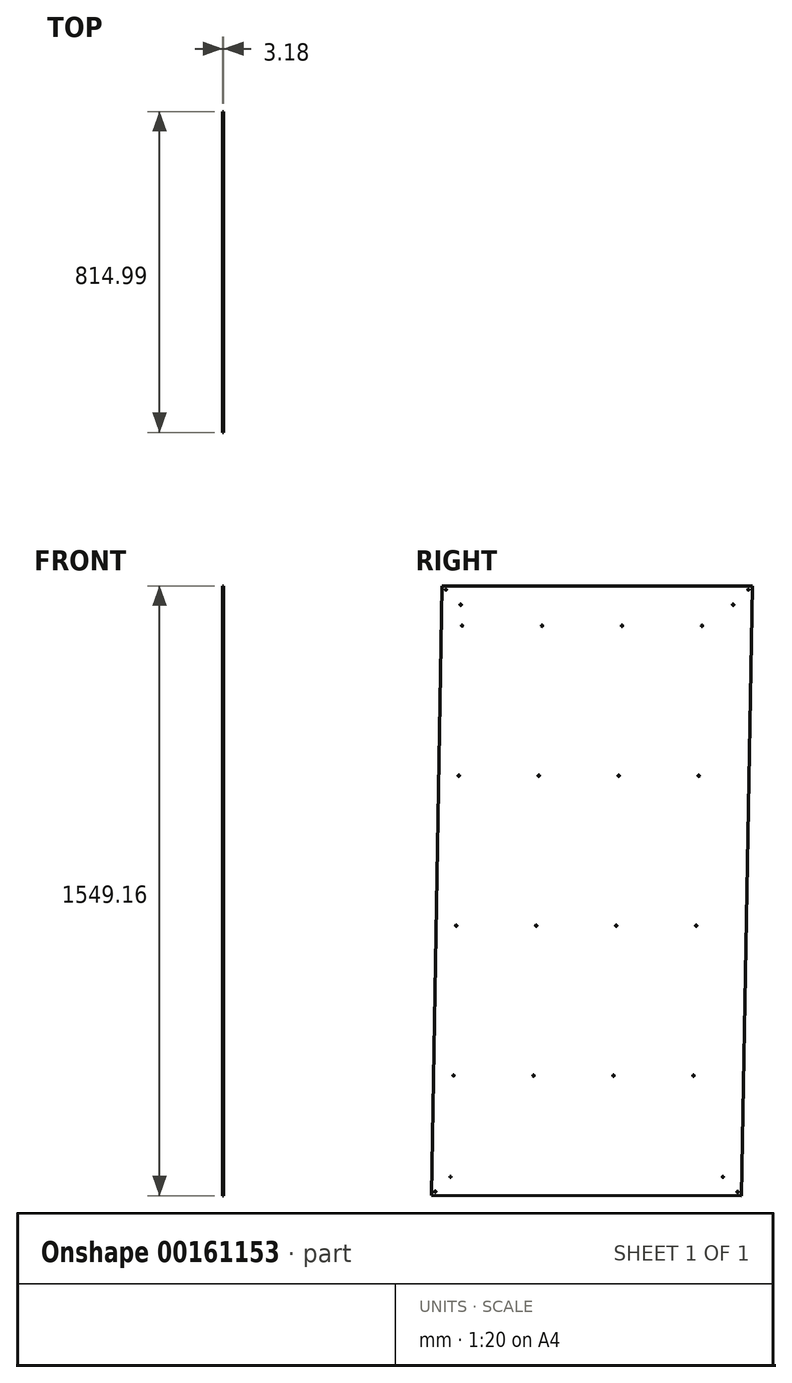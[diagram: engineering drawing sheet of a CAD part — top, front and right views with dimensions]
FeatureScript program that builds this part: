
annotation { "Feature Type Name" : "Feature", "Feature Type Description" : "" }
export const myFeature = defineFeature(function(context is Context, id is Id, definition is map)
    precondition{}
    {
        {
            var Q0;
            Q0=qCreatedBy(makeId("Right.planeOp"),FACE);
            var sketch = newSketch(context, id + "F0", { "sketchPlane" : qUnion([Q0])});
            skLineSegment(sketch, "E0.bottom", {"start": v(-392.5, 774.76) * mm, "end": v(394.9, 774.76) * mm});
            skLineSegment(sketch, "E0.left", {"start": v(-392.5, 774.76) * mm, "end": v(-420.09, -773.92) * mm});
            skLineSegment(sketch, "E0.right", {"start": v(394.9, 774.76) * mm, "end": v(367.3, -774.4) * mm});
            skLineSegment(sketch, "E1", {"start": v(367.3, -774.4) * mm, "end": v(-420.09, -773.92) * mm});
            skCircle(sketch, "E2", {"center": v(-383.14, 765.23) * mm, "radius": 1.59 * mm});
            skCircle(sketch, "E3", {"center": v(-345.71, 727.13) * mm, "radius": 1.59 * mm});
            skCircle(sketch, "E4", {"center": v(-393.68, -774.68) * mm, "radius": 0.01 * mm});
            skCircle(sketch, "E5", {"center": v(-393.64, -774.65) * mm, "radius": 0.02 * mm});
            skCircle(sketch, "E6", {"center": v(-410.4, -764.4) * mm, "radius": 1.59 * mm});
            skCircle(sketch, "E7", {"center": v(-371.6, -726.33) * mm, "radius": 1.59 * mm});
            skCircle(sketch, "E8", {"center": v(385.2, 765.23) * mm, "radius": 1.59 * mm});
            skCircle(sketch, "E9", {"center": v(346.42, 727.13) * mm, "radius": 1.59 * mm});
            skCircle(sketch, "E10", {"center": v(357.95, -764.87) * mm, "radius": 1.59 * mm});
            skCircle(sketch, "E11", {"center": v(320.52, -726.75) * mm, "radius": 1.59 * mm});
            skCircle(sketch, "E12", {"center": v(-363.85, -469.16) * mm, "radius": 1.59 * mm});
            skCircle(sketch, "E13", {"center": v(-160.65, -469.28) * mm, "radius": 1.59 * mm});
            skCircle(sketch, "E14", {"center": v(42.55, -469.4) * mm, "radius": 1.59 * mm});
            skCircle(sketch, "E15", {"center": v(245.75, -469.53) * mm, "radius": 1.59 * mm});
            skCircle(sketch, "E16", {"center": v(-357.06, -88.22) * mm, "radius": 1.59 * mm});
            skCircle(sketch, "E17", {"center": v(-153.86, -88.28) * mm, "radius": 1.59 * mm});
            skCircle(sketch, "E18", {"center": v(49.34, -88.46) * mm, "radius": 1.59 * mm});
            skCircle(sketch, "E19", {"center": v(252.54, -88.59) * mm, "radius": 1.59 * mm});
            skCircle(sketch, "E20", {"center": v(-350.34, 292.78) * mm, "radius": 1.59 * mm});
            skCircle(sketch, "E21", {"center": v(-147.14, 292.72) * mm, "radius": 1.59 * mm});
            skCircle(sketch, "E22", {"center": v(56.06, 292.54) * mm, "radius": 1.59 * mm});
            skCircle(sketch, "E23", {"center": v(259.26, 292.41) * mm, "radius": 1.59 * mm});
            skCircle(sketch, "E24", {"center": v(-342.12, 673.78) * mm, "radius": 1.59 * mm});
            skCircle(sketch, "E25", {"center": v(-138.92, 673.63) * mm, "radius": 1.59 * mm});
            skCircle(sketch, "E26", {"center": v(64.28, 673.54) * mm, "radius": 1.59 * mm});
            skCircle(sketch, "E27", {"center": v(267.48, 673.41) * mm, "radius": 1.59 * mm});
            skSolve(sketch);
        }
        {
            var Q0;
            Q0=makeQuery(id+"F0.imprint","IMPRINT",FACE,{"disambiguationData":[TD([[makeQuery(id+"F0.imprint","IMPRINT",EDGE,{"derivedFrom":sQuery(id+"F0.wireOp",EDGE,"E0.bottom")}),-1.0]])]});
            extrude(context, id + "F1", {"entities" : qUnion([Q0]), "depth" : 3.17 * mm});
        }
    });
